# Revit family: Shower_Receptors-Willoughby-AS-ADA
name_source: partatom
category: Plumbing Fixtures
revit_build: Autodesk Revit 2014 (Build: 20130308_1515(x64)
units: mm (PartAtom-declared; Revit-internal decimal feet)

## types (2) — shared parameters
CW Connection = No
Default Elevation = 0' - 0"
HW Connection = No
Manufacturer = Willoughby Industries
Revision = A
Type Comments = Integral Trench Drain
URL = www.willoughby-ind.com
Vent Connection = No
Waste Connection = Yes
Waste DIA = 4"

## per-type parameters (varying)
| type | Aquasurf Solid Surface | Depth | Description | Model | Width | Width/2 |
| 36X36 (AS-S3840FA) | Solid Surface Acrylic Resin-Willoughby | 3' - 4 3/16" | 36x36 ADA Accessible Shower Pan | AS-S3840FA | 3' - 2 13/16" | 1' - 7 13/32" |
| 30X60 (AS-S3462FA) | Solid Surface Acrylic Resin-Willoughby(1) | 2' - 10 1/4" | 30x60 ADA Accessible Shower Pan | AS-S3462FA | 5' - 2 1/2" | 2' - 7 1/4" |

## geometry (parser evidence)
native form markers: Extrusion x2, Sweep x1
no freeform markers — native parametric forms only
